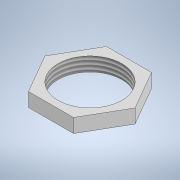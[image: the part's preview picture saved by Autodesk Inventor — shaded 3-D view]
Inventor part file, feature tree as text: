
AUTODESK INVENTOR PART (.ipt)
format: ipt  version: 2021 (Build 250183000, 183)  size: 107,520 bytes
history: native  units: mm
features: extrude x1, thread x1, sketch x1
ambient origin geometry x8: Origin, YZ Plane, XZ Plane, XY Plane, X Axis, Y Axis, Z Axis, Center Point
bodies: Solid1 (feature_tree)
feature tree (3):
  extrude  "Extrusion1"  Depth=2.5mm
  thread  "Thread1"  [1 undecoded]
  sketch  "Sketch1"  dims[d0=14.0mm d1=11.45mm d2=2.5mm d3=0.0mm d4=12.5mm d5=0.0mm]
note: 1 required parameter value undecoded (feature->parameter linkage not recoverable at this tier; creation-order binding heuristic only, values carry confidence <= 0.55)
